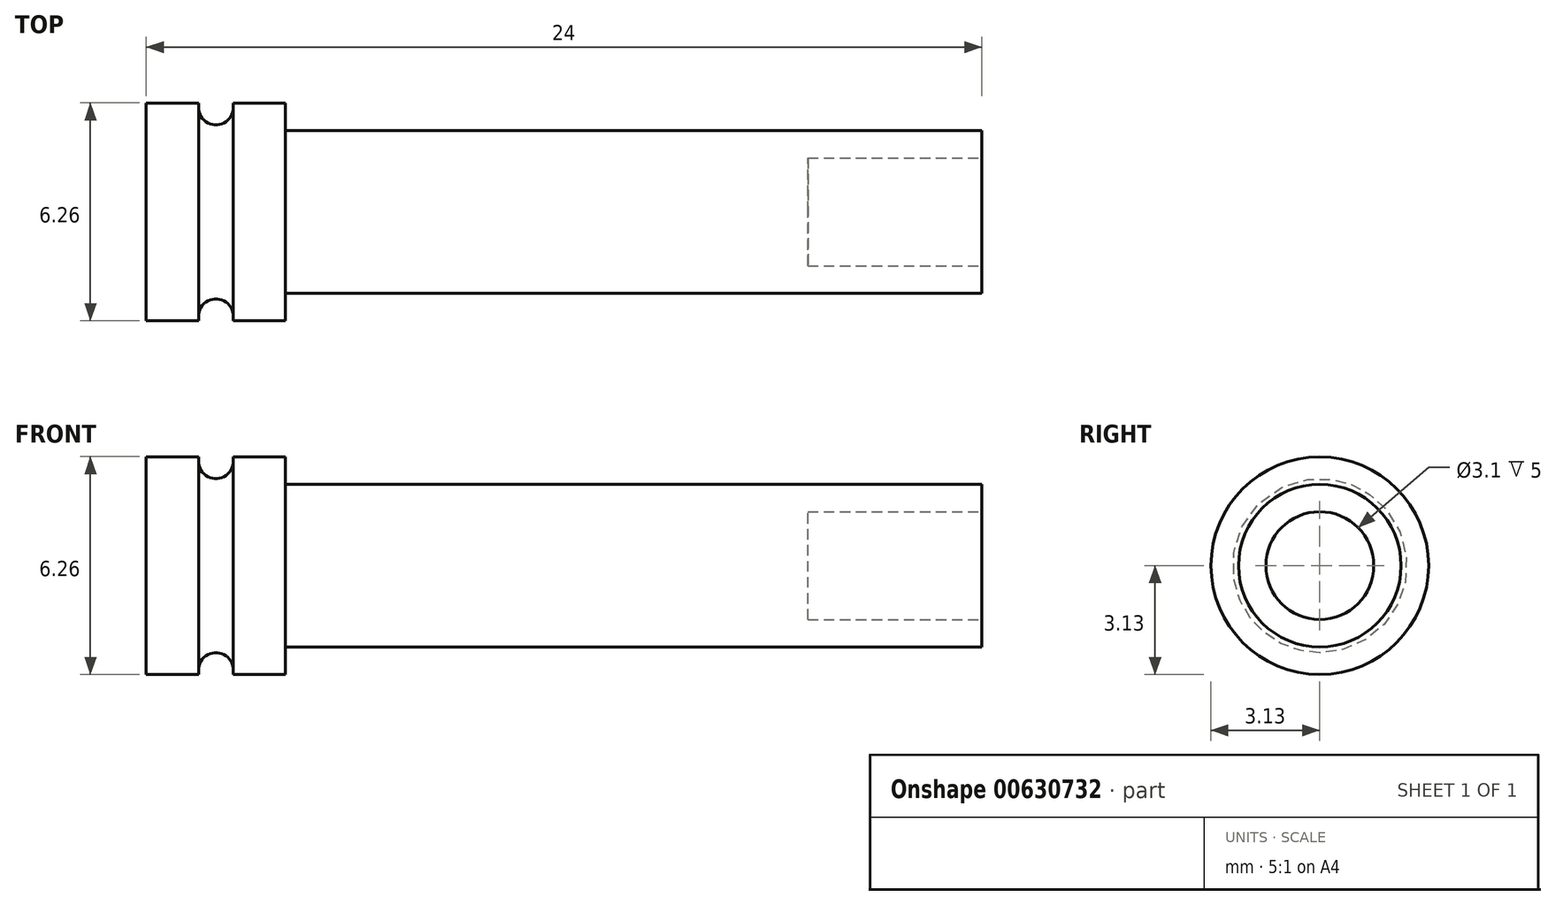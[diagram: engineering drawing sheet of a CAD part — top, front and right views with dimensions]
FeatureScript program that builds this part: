
annotation { "Feature Type Name" : "Feature", "Feature Type Description" : "" }
export const myFeature = defineFeature(function(context is Context, id is Id, definition is map)
    precondition{}
    {
        {
            var Q0;
            Q0=qCreatedBy(makeId("Right.planeOp"),FACE);
            var sketch = newSketch(context, id + "F0", { "sketchPlane" : qUnion([Q0])});
            skCircle(sketch, "E0", {"center": v(0, 0) * mm, "radius": 2.34 * mm});
            skSolve(sketch);
        }
        {
            var Q0;
            Q0=makeQuery(id+"F0.imprint","IMPRINT",FACE,{"disambiguationData":[TD([[makeQuery(id+"F0.imprint","IMPRINT",EDGE,{"derivedFrom":sQuery(id+"F0.wireOp",EDGE,"E0")}),1.0]])]});
            extrude(context, id + "F1", {"entities" : qUnion([Q0]), "depth" : 20 * mm, "offsetDistance" : 25 * mm});
        }
        {
            var Q0;
            Q0=makeQuery(id+"F1.opExtrude","CAP_FACE",FACE,{"disambiguationData":[OSD([sQuery(id+"F0.wireOp",EDGE,"E0")])],"isStart":true});
            var sketch = newSketch(context, id + "F2", { "sketchPlane" : qUnion([Q0])});
            skCircle(sketch, "E1", {"center": v(0, 0) * mm, "radius": 3.12 * mm});
            skSolve(sketch);
        }
        {
            var Q0;
            Q0 = qSketchRegion(id + "F2", true);
            extrude(context, id + "F3", {"entities" : qUnion([Q0]), "operationType" : NewBodyOperationType.ADD, "depth" : 4 * mm, "offsetDistance" : 25 * mm});
        }
        {
            var Q0;
            Q0=qCreatedBy(makeId("Front.planeOp"),FACE);
            var sketch = newSketch(context, id + "F4", { "sketchPlane" : qUnion([Q0])});
            skArc(sketch, "E2", {"start": v(-2.5, 3) * mm, "mid": v(-2, 2.5) * mm, "end": v(-1.5, 3) * mm});
            skLineSegment(sketch, "E3.bottom", {"start": v(-2.5, 3) * mm, "end": v(-1.5, 3) * mm});
            skLineSegment(sketch, "E3.top", {"start": v(-2.5, 4.44) * mm, "end": v(-1.5, 4.44) * mm});
            skLineSegment(sketch, "E3.left", {"start": v(-2.5, 3) * mm, "end": v(-2.5, 4.44) * mm});
            skLineSegment(sketch, "E3.right", {"start": v(-1.5, 3) * mm, "end": v(-1.5, 4.44) * mm});
            skLineSegment(sketch, "E4", {"start": v(-6.96, 0) * mm, "end": v(3.47, 0) * mm, "construction": true});
            skSolve(sketch);
        }
        {
            var Q0;
            Q0 = qSketchRegion(id + "F4", true);
            var Q1;
            Q1=sQuery(id+"F4.wireOp",EDGE,"E4");
            revolve(context, id + "F5", {"operationType" : NewBodyOperationType.REMOVE, "entities" : qUnion([Q0]), "axis" : qUnion([Q1]), "revolveType" : RevolveType.FULL, "oppositeDirection" : true});
        }
        {
            var Q0;
            Q0=makeQuery(id+"F1.opExtrude","CAP_FACE",FACE,{"disambiguationData":[OSD([sQuery(id+"F0.wireOp",EDGE,"E0")])],"isStart":false});
            var sketch = newSketch(context, id + "F6", { "sketchPlane" : qUnion([Q0])});
            skCircle(sketch, "E5", {"center": v(0, 0) * mm, "radius": 1.55 * mm});
            skSolve(sketch);
        }
        {
            var Q0;
            Q0=makeQuery(id+"F6.imprint","IMPRINT",FACE,{"disambiguationData":[TD([[makeQuery(id+"F6.imprint","IMPRINT",EDGE,{"derivedFrom":sQuery(id+"F6.wireOp",EDGE,"E5")}),1.0]])]});
            extrude(context, id + "F7", {"entities" : qUnion([Q0]), "operationType" : NewBodyOperationType.REMOVE, "oppositeDirection" : true, "depth" : 5 * mm, "offsetDistance" : 25 * mm});
        }
    });
